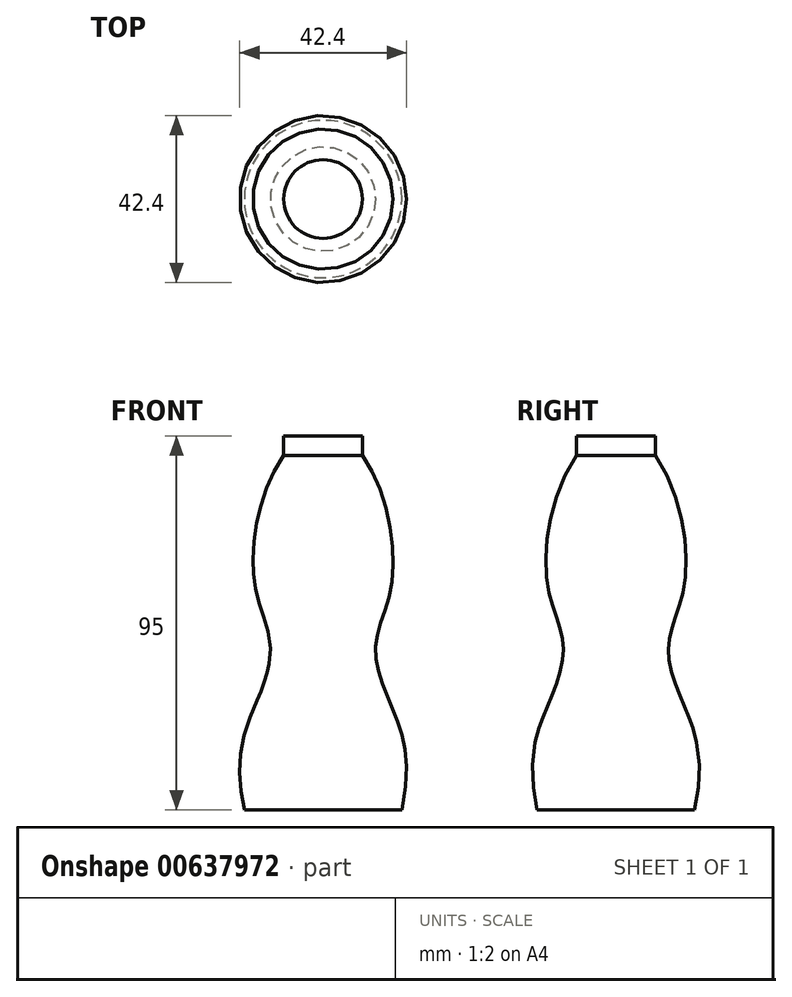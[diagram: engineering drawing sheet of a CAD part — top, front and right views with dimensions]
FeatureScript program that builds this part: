
annotation { "Feature Type Name" : "Feature", "Feature Type Description" : "" }
export const myFeature = defineFeature(function(context is Context, id is Id, definition is map)
    precondition{}
    {
        {
            var Q0;
            Q0=qCreatedBy(makeId("Front.planeOp"),FACE);
            var sketch = newSketch(context, id + "F0", { "sketchPlane" : qUnion([Q0])});
            skLineSegment(sketch, "E0", {"start": v(0, -26.48) * mm, "end": v(-20, -26.48) * mm});
            skLineSegment(sketch, "E1", {"start": v(-10, 63.52) * mm, "end": v(-10, 68.52) * mm});
            skLineSegment(sketch, "E2", {"start": v(-10, 68.52) * mm, "end": v(0, 68.52) * mm});
            skLineSegment(sketch, "E3", {"start": v(0, 68.52) * mm, "end": v(0, -26.48) * mm});
            skFitSpline(sketch, "E4", {"points": [v(-20, -26.48) * mm, v(-17.28, 0) * mm, v(-13.36, 15.22) * mm, v(-17.5, 31.6) * mm, v(-10, 63.52) * mm], "startDerivative": vector(-31.58, 150.22) * mm, "endDerivative": vector(61.56, 84.37) * mm});
            skSolve(sketch);
        }
        {
            var Q0;
            Q0 = qSketchRegion(id + "F0", true);
            var Q1;
            Q1=sQuery(id+"F0.wireOp",EDGE,"E3");
            revolve(context, id + "F1", {"entities" : qUnion([Q0]), "axis" : qUnion([Q1]), "revolveType" : RevolveType.FULL});
        }
    });
